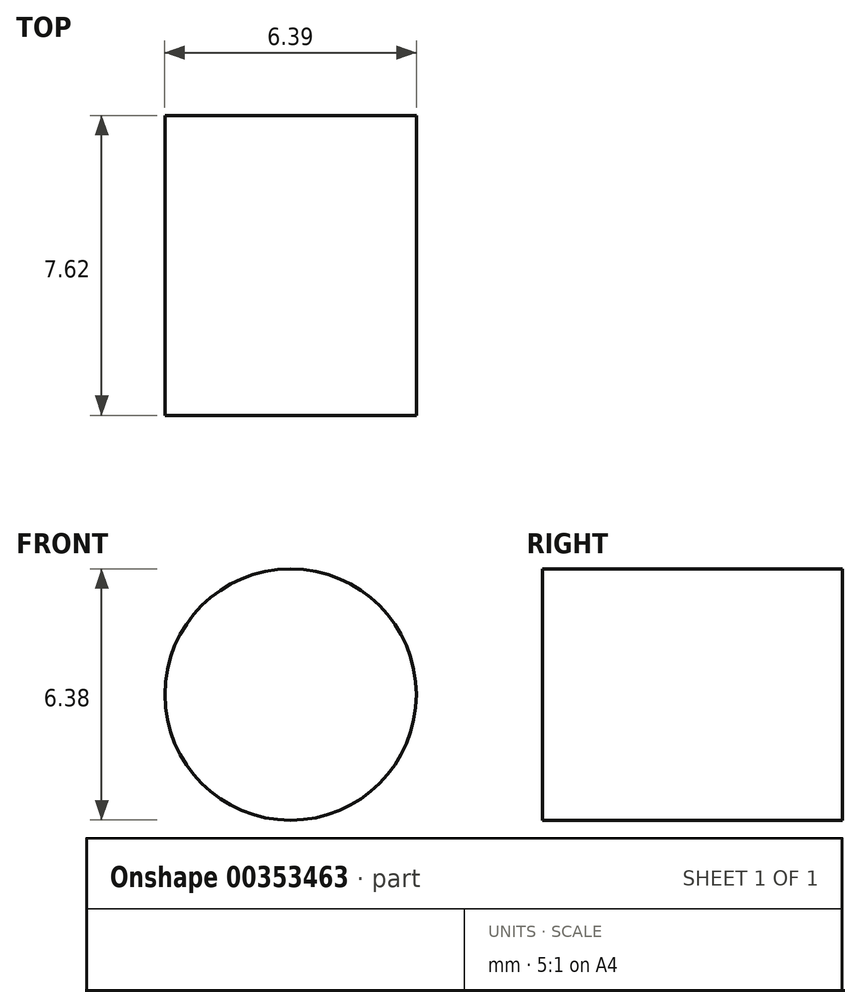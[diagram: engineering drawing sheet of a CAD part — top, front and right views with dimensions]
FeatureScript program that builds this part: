
annotation { "Feature Type Name" : "Feature", "Feature Type Description" : "" }
export const myFeature = defineFeature(function(context is Context, id is Id, definition is map)
    precondition{}
    {
        {
            var Q0;
            Q0=qCreatedBy(makeId("Front.planeOp"),FACE);
            var sketch = newSketch(context, id + "F0", { "sketchPlane" : qUnion([Q0])});
            skCircle(sketch, "E0", {"center": v(-53.05, 47.5) * mm, "radius": 3.2 * mm});
            skSolve(sketch);
        }
        {
            var Q0;
            Q0 = qSketchRegion(id + "F0", true);
            extrude(context, id + "F1", {"entities" : qUnion([Q0]), "depth" : 7.62 * mm});
        }
    });
